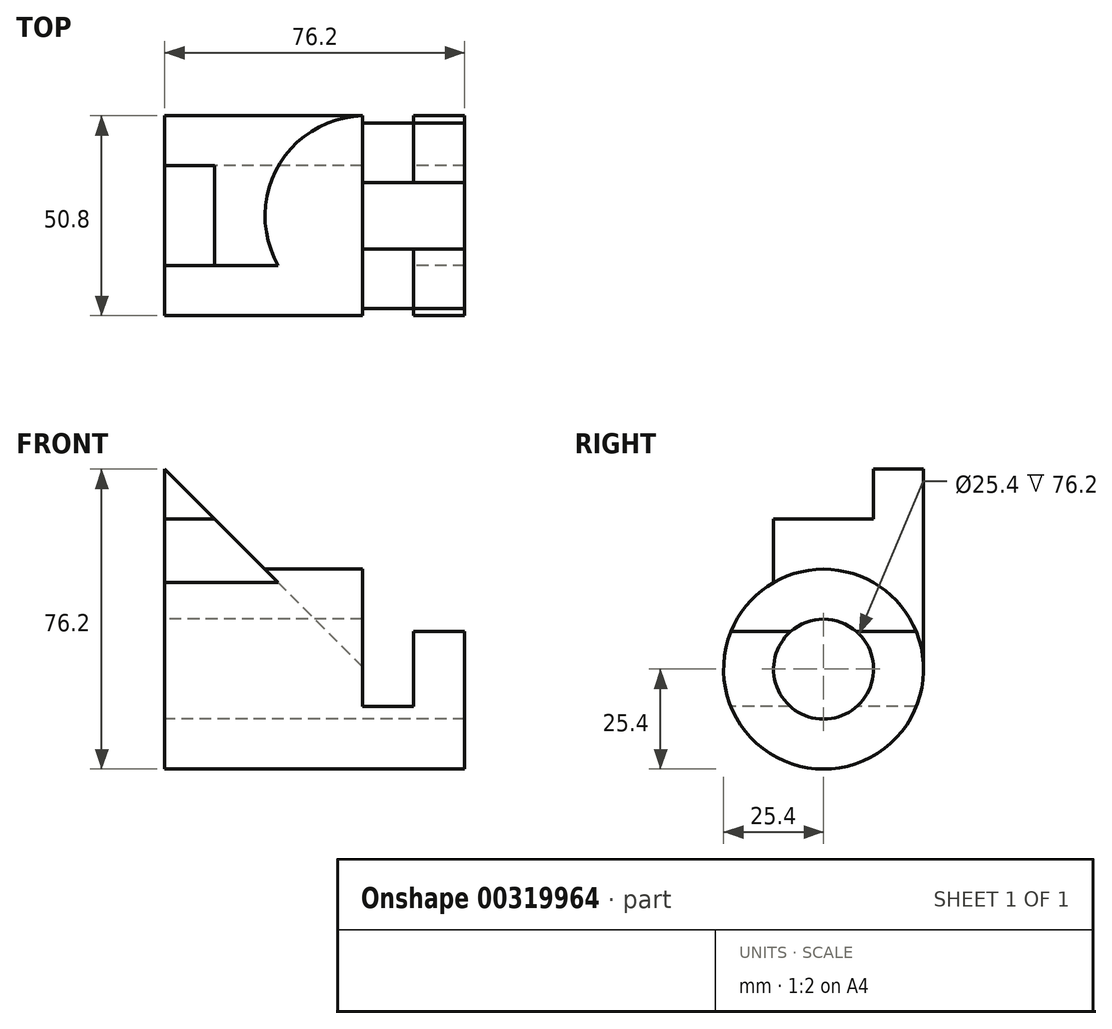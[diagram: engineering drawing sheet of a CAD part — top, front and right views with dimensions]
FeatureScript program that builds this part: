
annotation { "Feature Type Name" : "Feature", "Feature Type Description" : "" }
export const myFeature = defineFeature(function(context is Context, id is Id, definition is map)
    precondition{}
    {
        {
            var Q0;
            Q0=qCreatedBy(makeId("Right.planeOp"),FACE);
            var sketch = newSketch(context, id + "F0", { "sketchPlane" : qUnion([Q0])});
            skCircle(sketch, "E0", {"center": v(0, 0) * mm, "radius": 25.4 * mm});
            skCircle(sketch, "E1", {"center": v(0, 0) * mm, "radius": 12.7 * mm});
            skSolve(sketch);
        }
        {
            var Q0;
            Q0=qCreatedBy(makeId("Front.planeOp"),FACE);
            cPlane(context, id + "F1", {"entities" : qUnion([Q0]), "cplaneType" : CPlaneType.OFFSET, "offset" : 47.5 * mm, "width" : 152.4 * mm, "height" : 152.4 * mm});
        }
        {
            var Q0;
            Q0=qCreatedBy(makeId("Right.planeOp"),FACE);
            var sketch = newSketch(context, id + "F2", { "sketchPlane" : qUnion([Q0])});
            skCircle(sketch, "E2", {"center": v(0, 0) * mm, "radius": 25.4 * mm});
            skLineSegment(sketch, "E3", {"start": v(25.4, 0) * mm, "end": v(25.4, 50.8) * mm});
            skLineSegment(sketch, "E4", {"start": v(25.4, 50.8) * mm, "end": v(12.7, 50.8) * mm});
            skLineSegment(sketch, "E5", {"start": v(12.7, 50.8) * mm, "end": v(12.7, 38.1) * mm});
            skLineSegment(sketch, "E6", {"start": v(12.7, 38.1) * mm, "end": v(-12.7, 38.1) * mm});
            skLineSegment(sketch, "E7", {"start": v(-12.7, 38.1) * mm, "end": v(-12.7, 22) * mm});
            skSolve(sketch);
        }
        {
            var Q0;
            Q0=qCreatedBy(id+"F1.planeOp",FACE);
            var sketch = newSketch(context, id + "F3", { "sketchPlane" : qUnion([Q0])});
            skLineSegment(sketch, "E8", {"start": v(76.2, 9.53) * mm, "end": v(63.21, 9.53) * mm});
            skLineSegment(sketch, "E9", {"start": v(63.21, 9.53) * mm, "end": v(63.21, -9.53) * mm});
            skLineSegment(sketch, "E10", {"start": v(63.21, -9.53) * mm, "end": v(50.2, -9.53) * mm});
            skLineSegment(sketch, "E11", {"start": v(50.2, -9.53) * mm, "end": v(50.2, 31.14) * mm});
            skLineSegment(sketch, "E12", {"start": v(50.2, 31.14) * mm, "end": v(42.16, 31.14) * mm});
            skLineSegment(sketch, "E13", {"start": v(42.16, 31.14) * mm, "end": v(42.16, 41.38) * mm});
            skLineSegment(sketch, "E14", {"start": v(42.16, 41.38) * mm, "end": v(87.98, 41.38) * mm});
            skLineSegment(sketch, "E15", {"start": v(87.98, 41.38) * mm, "end": v(87.98, 0) * mm});
            skLineSegment(sketch, "E16", {"start": v(87.98, 0) * mm, "end": v(76.2, 0) * mm});
            skLineSegment(sketch, "E17", {"start": v(76.2, 0) * mm, "end": v(76.2, 9.53) * mm});
            skSolve(sketch);
        }
        {
            var Q0;
            {var subQ0=sQuery(id+"F2.wireOp",EDGE,"E3");Q0=makeQuery(id+"F2.imprint","IMPRINT",FACE,{"disambiguationData":[TD([[makeQuery(id+"F2.imprint","IMPRINT",EDGE,{"derivedFrom":subQ0}),1.0]])]});}
            extrude(context, id + "F4", {"entities" : qUnion([Q0]), "depth" : 50.8 * mm});
        }
        {
            var Q0;
            Q0=qCreatedBy(id+"F1.planeOp",FACE);
            var sketch = newSketch(context, id + "F5", { "sketchPlane" : qUnion([Q0])});
            skLineSegment(sketch, "E18", {"start": v(0, 50.8) * mm, "end": v(50.8, 0) * mm});
            skLineSegment(sketch, "E19", {"start": v(50.8, 0) * mm, "end": v(50.8, 50.8) * mm});
            skLineSegment(sketch, "E20", {"start": v(50.8, 50.8) * mm, "end": v(0, 50.8) * mm});
            skSolve(sketch);
        }
        {
            var Q0;
            Q0=makeQuery(id+"F5.imprint","IMPRINT",FACE,{"disambiguationData":[TD([[makeQuery(id+"F5.imprint","IMPRINT",EDGE,{"derivedFrom":sQuery(id+"F5.wireOp",EDGE,"E18")}),1.0]])]});
            extrude(context, id + "F6", {"entities" : qUnion([Q0]), "operationType" : NewBodyOperationType.REMOVE, "endBound" : BoundingType.THROUGH_ALL, "oppositeDirection" : true, "depth" : 25.4 * mm});
        }
        {
            var Q0;
            Q0 = qSketchRegion(id + "F0", true);
            extrude(context, id + "F7", {"entities" : qUnion([Q0]), "operationType" : NewBodyOperationType.ADD, "depth" : 76.2 * mm});
        }
        {
            var Q0;
            Q0=makeQuery(id+"F3.imprint","IMPRINT",FACE,{"disambiguationData":[TD([[makeQuery(id+"F3.imprint","IMPRINT",EDGE,{"derivedFrom":sQuery(id+"F3.wireOp",EDGE,"E8")}),-1.0]])]});
            extrude(context, id + "F8", {"entities" : qUnion([Q0]), "operationType" : NewBodyOperationType.REMOVE, "endBound" : BoundingType.THROUGH_ALL, "oppositeDirection" : true, "depth" : 25.4 * mm});
        }
    });
